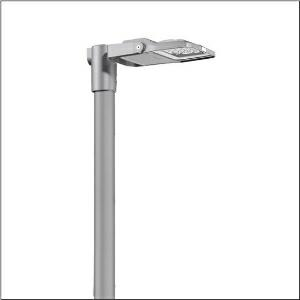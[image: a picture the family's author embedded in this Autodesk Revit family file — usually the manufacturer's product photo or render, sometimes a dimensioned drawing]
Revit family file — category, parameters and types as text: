
# Revit family: floodlight_fl_21_micro___pl33t_5xa7762a2f3a_37f8
name_source: partatom
category: Lighting Fixtures
units: mm (PartAtom-declared; Revit-internal decimal feet)

## family parameters
Cut with Voids When Loaded = No
Host = Face
Light Source = No
Part Type = Normal
Room Calculation Point = No
Round Connector Dimension = Use Diameter
Shared = No

## types (1)
- --- (1 x LED, 2930 lm, 23.1 W, 3000K)
    Apparent Load = 23 VA
    CIE Flux Codes = 26 75 99 100 100
    Color Rendering = 70
    Color Temperature = 3000K
    Default Elevation = 1800 mm
    Description = Floodlight FL 21 micro, floodlight, primary light control with lens, of PMMA, primary optical cover: protective disc, of toughened safety glass, transparent, light distribution: PL33T, light emission: direct distribution, installation type: surface-mounted, LED, High Power LED, rated luminous flux: 2.930lm, luminous efficacy: 127lm/W, light colour: 730, colour temperature: 3000K, control gear: ECG iQ, control: Auto-Match, Temp-Guard, Night-Set, Smart-Wire, Desk-Remote (wireless, voltage-free reading and setting of iQ features in the workshop via application-optimized NFC function/RFID function), optimised constant luminous flux control (CLO 2.0), Street-Remote, with terminal, 6-pole, mains connection: 220..240V, AC, 50/60Hz, start of lifetime: 23W, end of lifetime: 24W, reduction: 11W, luminaire housing, of diecast aluminium, powder-coated, Siteco® metallic grey (DB 702S), corrosivity category C5 according to DIN EN ISO 12944, mast bracket, of steel, galvanised, powder-coated, Siteco® metallic grey (DB 702S), protection rating (complete): IP66, insulation class (complete): insulation class II (safety insulation), certification: CE, protection symbol: D, impact resistance: IK07, permissible operating ambient temperature: -40..+40°C, permissible operating ambient temperature for outdoor applications: -40..+50°C, standard: DIN EN 12944, packaging unit: 1 piece

Light Distribution: PL33T
    Height = 65 mm
    Lamp = 1 x LED
    Lamp Light Flux = 2930 lm
    Lamp Power = 23.1 W
    Lamp count = 1
    Length = 312 mm
    Luminous efficacy = 127 lm/W
    Manufacturer = Siteco
    ModVariant = No
    Model = 5XA7762A2F3A
    Number of Poles = 1
    OnlyDefault = Yes
    Power Factor = 1
    Product Name = Floodlight FL 21 micro | PL33T
    Product group = floodlight | pylon top
    ProductGroupID = 6101
    Protection Class = Protection class II
    Protection Degree = IP 66
    RLX_Detail_Level = 1
    RlxData = <blob elided: 101449 chars, md5=d4ba6d59>
    Socket = socket
    Standby Power = 0 W
    System Light Flux = 2930 lm
    System Power = 23 W
    Type Comments = factory setting: luminous flux: 100 % | dim-lin: 254 | 455 mA
    Type Image = l_1007121.jpg
    URL = http://relux.com
    VarID = @adj_058063
    Voltage = 0 V
    Weight = 0.00 kg
    Width = 230 mm

## geometry (parser evidence)
native form markers: Blend x4, Sweep x13
no freeform markers — native parametric forms only
